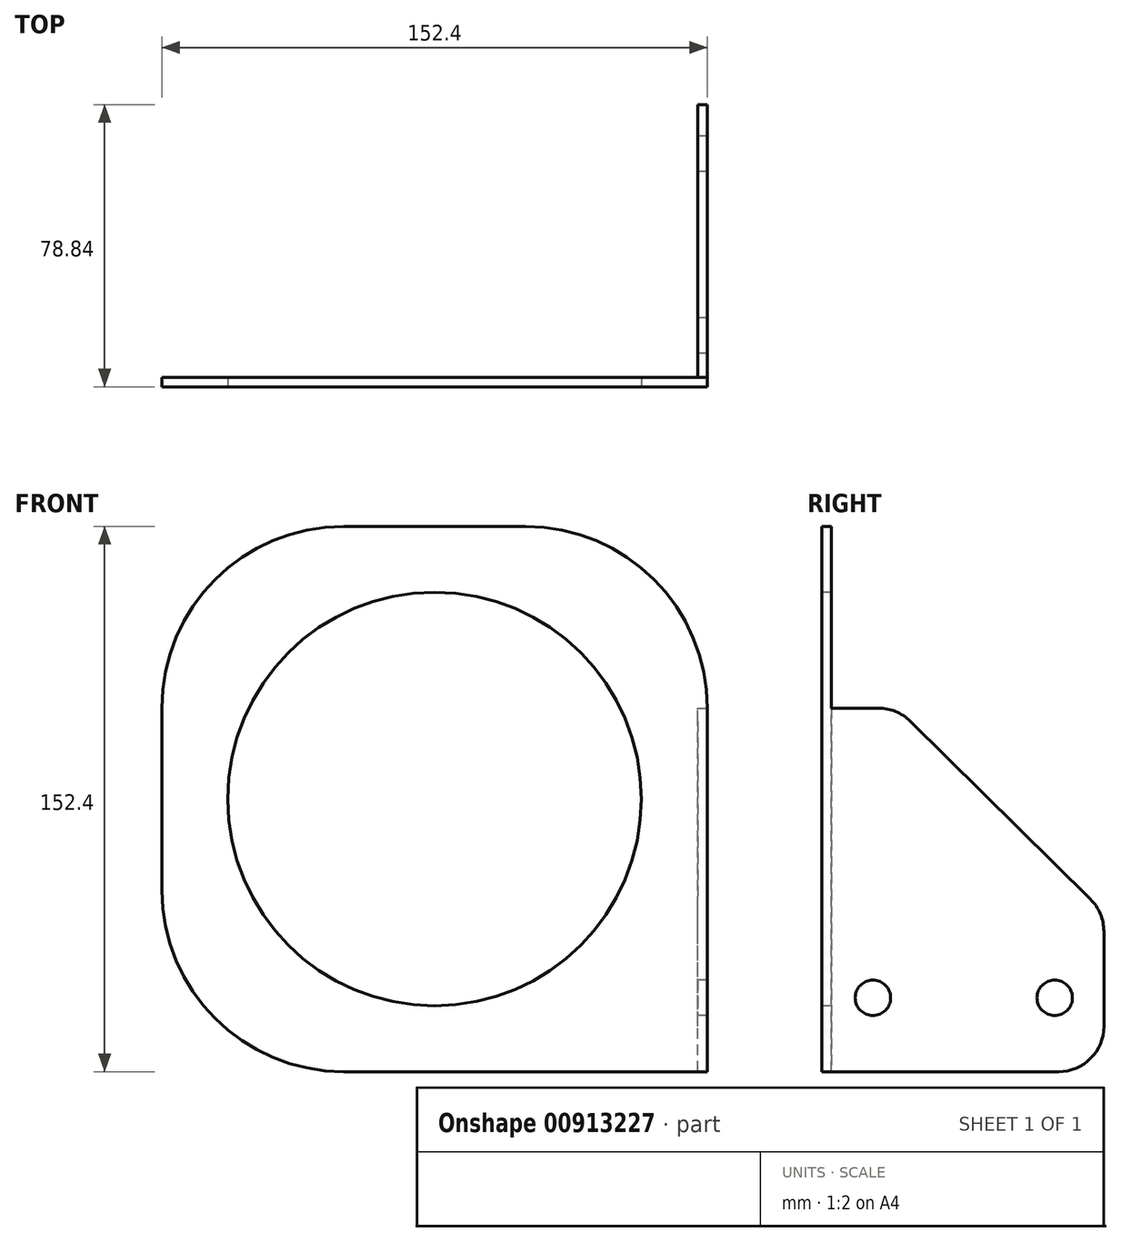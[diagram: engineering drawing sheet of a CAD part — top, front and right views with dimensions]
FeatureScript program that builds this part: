
annotation { "Feature Type Name" : "Feature", "Feature Type Description" : "" }
export const myFeature = defineFeature(function(context is Context, id is Id, definition is map)
    precondition{}
    {
        {
            var Q0;
            Q0=qCreatedBy(makeId("Front.planeOp"),FACE);
            var sketch = newSketch(context, id + "F0", { "sketchPlane" : qUnion([Q0])});
            skLineSegment(sketch, "E0.bottom", {"start": v(76.2, 76.2) * mm, "end": v(-76.2, 76.2) * mm});
            skLineSegment(sketch, "E0.top", {"start": v(76.2, -76.2) * mm, "end": v(-76.2, -76.2) * mm});
            skLineSegment(sketch, "E0.left", {"start": v(76.2, 76.2) * mm, "end": v(76.2, -76.2) * mm});
            skLineSegment(sketch, "E0.right", {"start": v(-76.2, 76.2) * mm, "end": v(-76.2, -76.2) * mm});
            skPoint(sketch, "E0.middle", {"position": v(0, 0) * mm});
            skSolve(sketch);
        }
        {
            var Q0;
            Q0 = qSketchRegion(id + "F0", true);
            extrude(context, id + "F1", {"entities" : qUnion([Q0]), "depth" : 2.64 * mm, "offsetDistance" : 25.4 * mm});
        }
        {
            var Q0;
            Q0=makeQuery(id+"F1.opExtrude","CAP_FACE",FACE,{"disambiguationData":[OSD([sQuery(id+"F0.wireOp",EDGE,"E0.bottom"),sQuery(id+"F0.wireOp",EDGE,"E0.top"),sQuery(id+"F0.wireOp",EDGE,"E0.left"),sQuery(id+"F0.wireOp",EDGE,"E0.right")])],"isStart":true});
            var sketch = newSketch(context, id + "F2", { "sketchPlane" : qUnion([Q0])});
            skLineSegment(sketch, "E1.bottom", {"start": v(-76.2, -76.2) * mm, "end": v(-73.56, -76.2) * mm});
            skLineSegment(sketch, "E1.top", {"start": v(-76.2, -31.75) * mm, "end": v(-73.56, -31.75) * mm});
            skLineSegment(sketch, "E1.left", {"start": v(-76.2, -76.2) * mm, "end": v(-76.2, -31.75) * mm});
            skLineSegment(sketch, "E1.right", {"start": v(-73.56, -76.2) * mm, "end": v(-73.56, -31.75) * mm});
            skSolve(sketch);
        }
        {
            var Q0;
            Q0 = qSketchRegion(id + "F2", true);
            extrude(context, id + "F3", {"entities" : qUnion([Q0]), "operationType" : NewBodyOperationType.ADD, "depth" : 76.2 * mm, "offsetDistance" : 25.4 * mm});
        }
        {
            var Q0;
            Q0=makeQuery(id+"F1.opExtrude","CAP_FACE",FACE,{"disambiguationData":[OSD([sQuery(id+"F0.wireOp",EDGE,"E0.bottom"),sQuery(id+"F0.wireOp",EDGE,"E0.top"),sQuery(id+"F0.wireOp",EDGE,"E0.left"),sQuery(id+"F0.wireOp",EDGE,"E0.right")])],"isStart":false});
            var sketch = newSketch(context, id + "F4", { "sketchPlane" : qUnion([Q0])});
            skCircle(sketch, "E2", {"center": v(0, 0) * mm, "radius": 57.79 * mm});
            skSolve(sketch);
        }
        {
            var Q0;
            Q0 = qSketchRegion(id + "F4", true);
            extrude(context, id + "F5", {"entities" : qUnion([Q0]), "operationType" : NewBodyOperationType.REMOVE, "oppositeDirection" : true, "depth" : 25.4 * mm, "offsetDistance" : 25.4 * mm});
        }
        {
            var Q0;
            Q0=makeQuery(id+"F1.opExtrude","SWEPT_EDGE",EDGE,{"disambiguationData":[OSD([sQuery(id+"F0.wireOp",EDGE,"E0.bottom"),sQuery(id+"F0.wireOp",EDGE,"E0.left")])]});
            var Q1;
            Q1=makeQuery(id+"F1.opExtrude","SWEPT_EDGE",EDGE,{"disambiguationData":[OSD([sQuery(id+"F0.wireOp",EDGE,"E0.bottom"),sQuery(id+"F0.wireOp",EDGE,"E0.right")])]});
            var Q2;
            Q2=makeQuery(id+"F1.opExtrude","SWEPT_EDGE",EDGE,{"disambiguationData":[OSD([sQuery(id+"F0.wireOp",EDGE,"E0.top"),sQuery(id+"F0.wireOp",EDGE,"E0.right")])]});
            fillet(context, id + "F6", {"entities" : qUnion([Q0, Q1, Q2]), "radius" : 50.8 * mm, "tangentPropagation" : true, "allowEdgeOverflow" : false});
        }
        {
            var Q0;
            Q0=makeQuery(id+"F3.opExtrude","SWEPT_FACE",FACE,{"disambiguationData":[OSD([sQuery(id+"F2.wireOp",EDGE,"E1.right")])]});
            var sketch = newSketch(context, id + "F7", { "sketchPlane" : qUnion([Q0])});
            skCircle(sketch, "E3", {"center": v(-11.66, -55.56) * mm, "radius": 4.95 * mm});
            skCircle(sketch, "E4", {"center": v(-62.46, -55.56) * mm, "radius": 4.95 * mm});
            skSolve(sketch);
        }
        {
            var Q0;
            Q0 = qSketchRegion(id + "F7", true);
            extrude(context, id + "F8", {"entities" : qUnion([Q0]), "operationType" : NewBodyOperationType.REMOVE, "oppositeDirection" : true, "depth" : 25.4 * mm, "offsetDistance" : 25.4 * mm});
        }
        {
            var Q0;
            Q0=makeQuery(id+"F3.boolean.opBoolean","MERGE",FACE,{"derivedFrom":[makeQuery(id+"F1.opExtrude","SWEPT_FACE",FACE,{"disambiguationData":[OSD([sQuery(id+"F0.wireOp",EDGE,"E0.left")])]}),makeQuery(id+"F3.opExtrude","SWEPT_FACE",FACE,{"disambiguationData":[OSD([sQuery(id+"F2.wireOp",EDGE,"E1.left")])]})]});
            var sketch = newSketch(context, id + "F9", { "sketchPlane" : qUnion([Q0])});
            skLineSegment(sketch, "E5", {"start": v(0, 25.4) * mm, "end": v(18.4, 25.4) * mm});
            skLineSegment(sketch, "E6", {"start": v(18.4, 25.4) * mm, "end": v(76.2, -31.75) * mm});
            skLineSegment(sketch, "E7", {"start": v(0, 25.4) * mm, "end": v(0, -31.75) * mm});
            skLineSegment(sketch, "E8", {"start": v(0, -31.75) * mm, "end": v(76.2, -31.75) * mm});
            skSolve(sketch);
        }
        {
            var Q0;
            Q0 = qSketchRegion(id + "F9", true);
            extrude(context, id + "F10", {"entities" : qUnion([Q0]), "operationType" : NewBodyOperationType.ADD, "oppositeDirection" : true, "depth" : 2.64 * mm, "offsetDistance" : 25.4 * mm});
        }
        {
            var Q0;
            Q0=makeQuery(id+"F3.opExtrude","CAP_EDGE",EDGE,{"disambiguationData":[OSD([sQuery(id+"F2.wireOp",EDGE,"E1.bottom")])],"isStart":false});
            var Q1;
            Q1=makeQuery(id+"F3.opExtrude","CAP_EDGE",EDGE,{"disambiguationData":[OSD([sQuery(id+"F2.wireOp",EDGE,"E1.top")])],"isStart":false});
            var Q2;
            Q2=makeQuery(id+"F10.opExtrude","SWEPT_EDGE",EDGE,{"disambiguationData":[OSD([sQuery(id+"F9.wireOp",EDGE,"E5"),sQuery(id+"F9.wireOp",EDGE,"E6")])]});
            fillet(context, id + "F11", {"entities" : qUnion([Q0, Q1, Q2]), "radius" : 12.7 * mm, "tangentPropagation" : true, "allowEdgeOverflow" : false});
        }
    });
